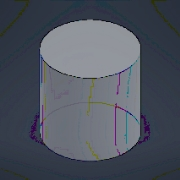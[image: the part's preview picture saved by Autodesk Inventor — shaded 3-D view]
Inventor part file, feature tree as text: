
AUTODESK INVENTOR PART (.ipt)
format: ipt  version: 2024.3 (Build 283343000, 343)  size: 134,144 bytes
history: native  units: mm
features: extrude x1, sketch x1
ambient origin geometry x8: Origin, YZ Plane, XZ Plane, XY Plane, X Axis, Y Axis, Z Axis, Center Point
bodies: Solid1 (feature_tree)
feature tree (2):
  extrude  "Extrusion1"  [1 undecoded]
  sketch  "Sketch1"  dims[d1=70.0mm d2=0.0mm]
note: 1 required parameter value undecoded (feature->parameter linkage not recoverable at this tier; creation-order binding heuristic only, values carry confidence <= 0.55)
